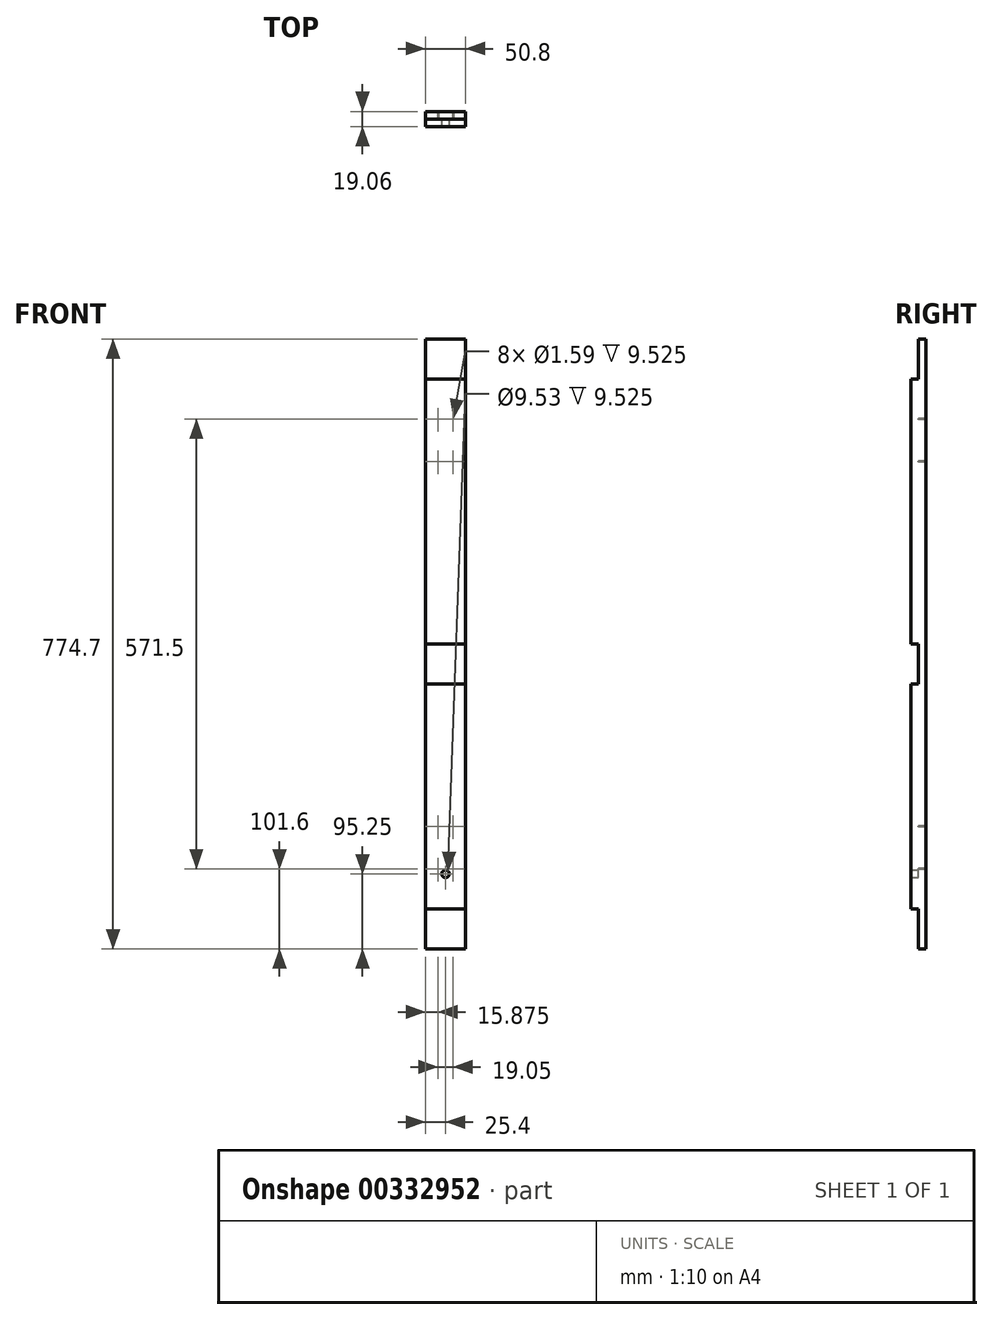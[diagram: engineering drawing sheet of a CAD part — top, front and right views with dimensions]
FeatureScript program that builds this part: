
annotation { "Feature Type Name" : "Feature", "Feature Type Description" : "" }
export const myFeature = defineFeature(function(context is Context, id is Id, definition is map)
    precondition{}
    {
        {
            var Q0;
            Q0=qCreatedBy(makeId("Top.planeOp"),FACE);
            var sketch = newSketch(context, id + "F0", { "sketchPlane" : qUnion([Q0])});
            skLineSegment(sketch, "E0.bottom", {"start": v(25.4, 9.53) * mm, "end": v(-25.4, 9.53) * mm});
            skLineSegment(sketch, "E0.top", {"start": v(25.4, -9.53) * mm, "end": v(-25.4, -9.53) * mm});
            skLineSegment(sketch, "E0.left", {"start": v(25.4, 9.53) * mm, "end": v(25.4, -9.52) * mm});
            skLineSegment(sketch, "E0.right", {"start": v(-25.4, 9.53) * mm, "end": v(-25.4, -9.53) * mm});
            skPoint(sketch, "E0.middle", {"position": v(0, 0) * mm});
            skSolve(sketch);
        }
        {
            var Q0;
            Q0=makeQuery(id+"F0.imprint","IMPRINT",FACE,{"disambiguationData":[TD([[makeQuery(id+"F0.imprint","IMPRINT",EDGE,{"derivedFrom":sQuery(id+"F0.wireOp",EDGE,"E0.bottom")}),1.0]])]});
            var Q1;
            Q1=qSketchRegion(id+"F2",true);
            extrude(context, id + "F1", {"entities" : qUnion([Q0, Q1]), "depth" : 774.7 * mm});
        }
        {
            var Q0;
            Q0=qCreatedBy(makeId("Front.planeOp"),FACE);
            var sketch = newSketch(context, id + "F2", { "sketchPlane" : qUnion([Q0])});
            skLineSegment(sketch, "E1.bottom", {"start": v(-38.77, 0) * mm, "end": v(83.66, 0) * mm});
            skLineSegment(sketch, "E1.top", {"start": v(-38.77, 50.8) * mm, "end": v(83.66, 50.8) * mm});
            skLineSegment(sketch, "E1.left", {"start": v(-38.77, 0) * mm, "end": v(-38.77, 50.8) * mm});
            skLineSegment(sketch, "E1.right", {"start": v(83.66, 0) * mm, "end": v(83.66, 50.8) * mm});
            skLineSegment(sketch, "E2.bottom", {"start": v(-210.36, 723.9) * mm, "end": v(132.8, 723.9) * mm});
            skLineSegment(sketch, "E2.top", {"start": v(-210.36, 774.7) * mm, "end": v(132.8, 774.7) * mm});
            skLineSegment(sketch, "E2.left", {"start": v(-210.36, 723.9) * mm, "end": v(-210.36, 774.7) * mm});
            skLineSegment(sketch, "E2.right", {"start": v(132.8, 723.9) * mm, "end": v(132.8, 774.7) * mm});
            skLineSegment(sketch, "E3.bottom", {"start": v(-179.92, 387.35) * mm, "end": v(84.62, 387.35) * mm});
            skLineSegment(sketch, "E3.top", {"start": v(-179.92, 336.55) * mm, "end": v(84.62, 336.55) * mm});
            skLineSegment(sketch, "E3.left", {"start": v(-179.92, 387.35) * mm, "end": v(-179.92, 336.55) * mm});
            skLineSegment(sketch, "E3.right", {"start": v(84.62, 387.35) * mm, "end": v(84.62, 336.55) * mm});
            skSolve(sketch);
        }
        {
            var Q0;
            Q0=qSketchRegion(id+"F2",true);
            extrude(context, id + "F3", {"entities" : qUnion([Q0]), "operationType" : NewBodyOperationType.REMOVE, "depth" : 25.4 * mm});
        }
        {
            var Q0;
            Q0=qCreatedBy(makeId("Front.planeOp"),FACE);
            var sketch = newSketch(context, id + "F4", { "sketchPlane" : qUnion([Q0])});
            skCircle(sketch, "E4", {"center": v(9.53, 101.6) * mm, "radius": 0.8 * mm});
            skCircle(sketch, "E5", {"center": v(9.52, 155.58) * mm, "radius": 0.8 * mm});
            skCircle(sketch, "E6", {"center": v(9.52, 619.12) * mm, "radius": 0.8 * mm});
            skCircle(sketch, "E7", {"center": v(9.52, 673.1) * mm, "radius": 0.8 * mm});
            skLineSegment(sketch, "E8", {"start": v(0, 0) * mm, "end": v(0, 1192.46) * mm, "construction": true});
            skLineSegment(sketch, "E9.bottom", {"start": v(9.52, 101.6) * mm, "end": v(-9.52, 101.6) * mm, "construction": true});
            skLineSegment(sketch, "E9.top", {"start": v(9.52, 673.1) * mm, "end": v(-9.53, 673.1) * mm, "construction": true});
            skLineSegment(sketch, "E9.left", {"start": v(9.53, 101.6) * mm, "end": v(9.52, 673.1) * mm, "construction": true});
            skLineSegment(sketch, "E9.right", {"start": v(-9.53, 101.6) * mm, "end": v(-9.53, 673.1) * mm, "construction": true});
            skCircle(sketch, "E10", {"center": v(-9.53, 619.12) * mm, "radius": 0.8 * mm});
            skCircle(sketch, "E11", {"center": v(-9.53, 673.1) * mm, "radius": 0.8 * mm});
            skCircle(sketch, "E12", {"center": v(-9.53, 101.6) * mm, "radius": 0.8 * mm});
            skCircle(sketch, "E13", {"center": v(-9.53, 155.58) * mm, "radius": 0.8 * mm});
            skSolve(sketch);
        }
        {
            var Q0;
            Q0=qSketchRegion(id+"F4",true);
            extrude(context, id + "F5", {"entities" : qUnion([Q0]), "operationType" : NewBodyOperationType.REMOVE, "oppositeDirection" : true, "depth" : 25.4 * mm});
        }
        {
            var Q0;
            Q0=qCreatedBy(makeId("Front.planeOp"),FACE);
            var sketch = newSketch(context, id + "F6", { "sketchPlane" : qUnion([Q0])});
            skCircle(sketch, "E14", {"center": v(0, 95.25) * mm, "radius": 4.76 * mm});
            skSolve(sketch);
        }
        {
            var Q0;
            Q0=qSketchRegion(id+"F6",true);
            extrude(context, id + "F7", {"entities" : qUnion([Q0]), "operationType" : NewBodyOperationType.REMOVE, "depth" : 25.4 * mm});
        }
    });
